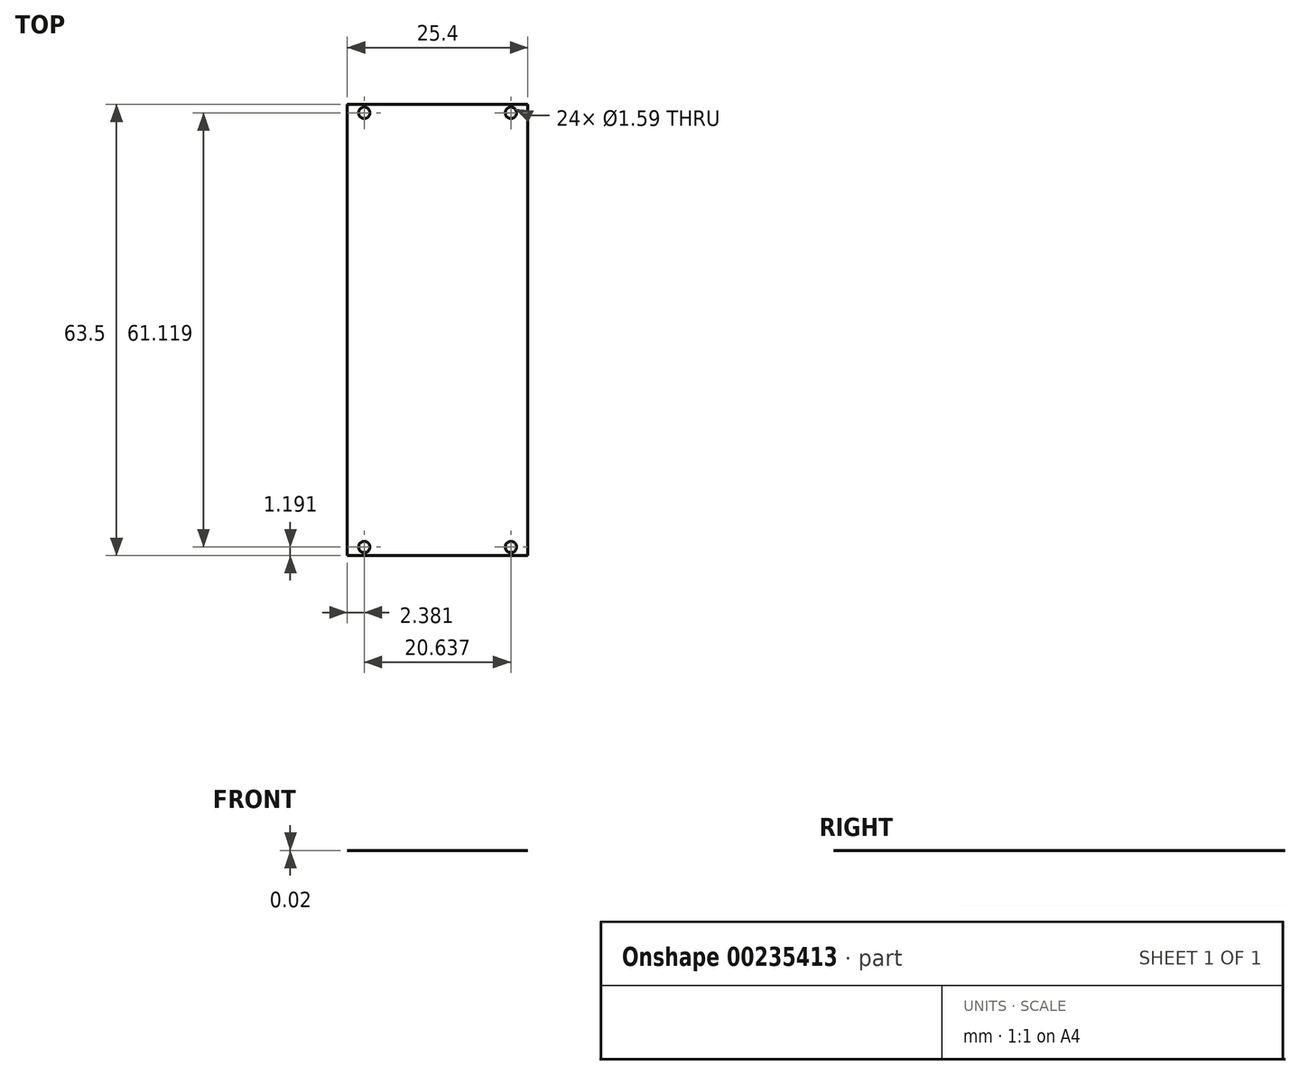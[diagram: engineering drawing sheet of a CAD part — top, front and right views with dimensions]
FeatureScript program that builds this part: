
annotation { "Feature Type Name" : "Feature", "Feature Type Description" : "" }
export const myFeature = defineFeature(function(context is Context, id is Id, definition is map)
    precondition{}
    {
        {
            var Q0;
            Q0=qCreatedBy(makeId("Top.planeOp"),FACE);
            var sketch = newSketch(context, id + "F0", { "sketchPlane" : qUnion([Q0])});
            skLineSegment(sketch, "E0.bottom", {"start": v(-12.7, 31.75) * mm, "end": v(12.7, 31.75) * mm});
            skLineSegment(sketch, "E0.top", {"start": v(-12.7, -31.75) * mm, "end": v(12.7, -31.75) * mm});
            skLineSegment(sketch, "E0.left", {"start": v(-12.7, 31.75) * mm, "end": v(-12.7, -31.75) * mm});
            skLineSegment(sketch, "E0.right", {"start": v(12.7, 31.75) * mm, "end": v(12.7, -31.75) * mm});
            skPoint(sketch, "E0.middle", {"position": v(0, 0) * mm});
            skLineSegment(sketch, "E1.bottom", {"start": v(-10.32, 30.56) * mm, "end": v(10.32, 30.56) * mm, "construction": true});
            skLineSegment(sketch, "E1.top", {"start": v(-10.32, -30.56) * mm, "end": v(10.32, -30.56) * mm, "construction": true});
            skCircle(sketch, "E2", {"center": v(-10.32, 30.56) * mm, "radius": 0.8 * mm});
            skCircle(sketch, "E3", {"center": v(10.32, 30.56) * mm, "radius": 0.8 * mm});
            skCircle(sketch, "E4", {"center": v(10.32, -30.56) * mm, "radius": 0.8 * mm});
            skCircle(sketch, "E5", {"center": v(-10.32, -30.56) * mm, "radius": 0.8 * mm});
            skLineSegment(sketch, "E6", {"start": v(0, 0) * mm, "end": v(0, 30.56) * mm, "construction": true});
            skSolve(sketch);
        }
        {
            var Q0;
            Q0=makeQuery(id+"F0.imprint","IMPRINT",FACE,{"disambiguationData":[TD([[makeQuery(id+"F0.imprint","IMPRINT",EDGE,{"derivedFrom":sQuery(id+"F0.wireOp",EDGE,"E0.bottom")}),-1.0]])]});
            extrude(context, id + "F1", {"entities" : qUnion([Q0]), "endBound" : BoundingType.SYMMETRIC, "depth" : 3 / 203.2 * mm});
        }
    });
